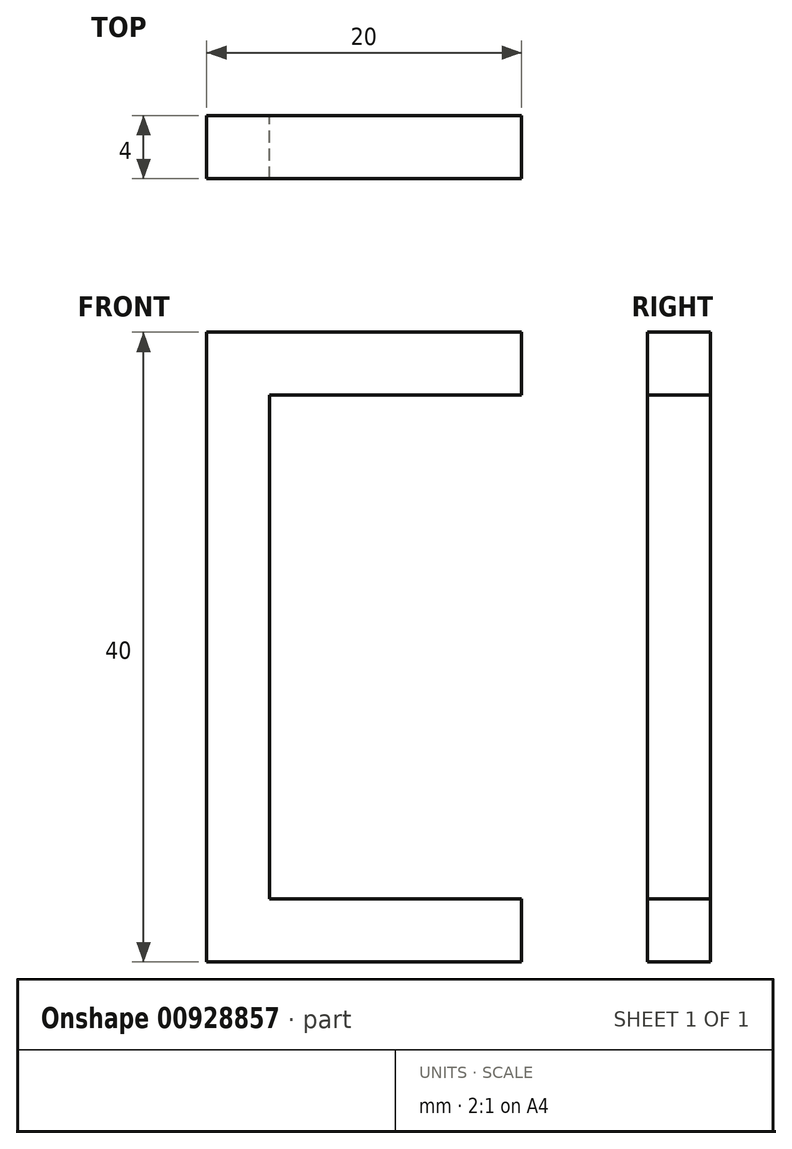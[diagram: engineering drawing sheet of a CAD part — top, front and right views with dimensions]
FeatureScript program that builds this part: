
annotation { "Feature Type Name" : "Feature", "Feature Type Description" : "" }
export const myFeature = defineFeature(function(context is Context, id is Id, definition is map)
    precondition{}
    {
        {
            var Q0;
            Q0=qCreatedBy(makeId("Front.planeOp"),FACE);
            var sketch = newSketch(context, id + "F0", { "sketchPlane" : qUnion([Q0])});
            skLineSegment(sketch, "E0", {"start": v(0, 0) * mm, "end": v(0, 20) * mm});
            skLineSegment(sketch, "E1", {"start": v(0, 20) * mm, "end": v(20, 20) * mm});
            skLineSegment(sketch, "E2", {"start": v(20, 20) * mm, "end": v(20, 16) * mm});
            skLineSegment(sketch, "E3", {"start": v(20, 16) * mm, "end": v(4, 16) * mm});
            skLineSegment(sketch, "E4", {"start": v(4, 16) * mm, "end": v(4, 0) * mm});
            skLineSegment(sketch, "E5", {"start": v(-7.13, 0) * mm, "end": v(8.3, 0) * mm, "construction": true});
            skLineSegment(sketch, "E6.MirrorCS", {"start": v(4, -16) * mm, "end": v(4, 0) * mm});
            skLineSegment(sketch, "E7.MirrorCS", {"start": v(0, 0) * mm, "end": v(0, -20) * mm});
            skLineSegment(sketch, "E8.MirrorCS", {"start": v(20, -16) * mm, "end": v(4, -16) * mm});
            skLineSegment(sketch, "E9.MirrorCS", {"start": v(20, -20) * mm, "end": v(20, -16) * mm});
            skLineSegment(sketch, "E10.MirrorCS", {"start": v(0, -20) * mm, "end": v(20, -20) * mm});
            skSolve(sketch);
        }
        {
            var Q0;
            Q0 = qSketchRegion(id + "F0", true);
            extrude(context, id + "F1", {"entities" : qUnion([Q0]), "depth" : 4 * mm, "offsetDistance" : 25 * mm});
        }
    });
